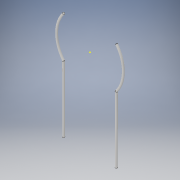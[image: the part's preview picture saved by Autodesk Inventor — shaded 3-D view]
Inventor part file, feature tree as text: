
AUTODESK INVENTOR PART (.ipt)
format: ipt  version: 2017 (Build 210142000, 142)  size: 131,584 bytes
history: native  units: in
note: dims shown in document units (in); Inventor stores cm internally (conversion verified against a paired STEP export)
features: sketch x8, plane x4, sweep x4
ambient origin geometry x8: Origin, YZ Plane, XZ Plane, XY Plane, X Axis, Y Axis, Z Axis, Center Point
bodies: Solid1 (feature_tree)
feature tree (16):
  sketch  "Sketch3"  dims[d3=8.013in d4=8.013in]
  sketch  "Sketch4"  dims[d5=0.25in d6=0.25in]
  sketch  "Sketch5"  dims[d7=0.0in d8=0.0in d9=0.0in d10=0.0in]
  plane  "Work Plane1"
  plane  "Work Plane2"
  sketch  "Sketch6"  dims[d11=0.25in d12=0.25in]
  plane  "Work Plane3"
  plane  "Work Plane4"
  sketch  "Sketch7"  dims[d13=0.0in d14=0.0in]
  sweep  "Sweep1"
  sweep  "Sweep2"
  sketch  "Sketch8"  dims[d15=0.0in d16=0.0in]
  sketch  "Sketch9"
  sweep  "Sweep3"
  sweep  "Sweep4"
  sketch  "Sketch10"
